# Revit family: XY 4 L
name_source: partatom
category: Generic Models
revit_build: Autodesk Revit 2017 (Build: 20170419_0315(x64)
units: mm (PartAtom-declared; Revit-internal decimal feet)

## family parameters
Always vertical = Yes
Can host rebar = No
Cut with Voids When Loaded = No
Host = Wall
Part Type = Normal
Room Calculation Point = No
Round Connector Dimension = Use Diameter
Shared = No

## types (1)
- XY 4 L
    Depth = 200 mm  [stored 0.656168 ft]
    EAN = 6430034743057
    Height = 870 mm
    IP = IP 34
    Keynote = 6120
    LVI = 5282083
    Leveys = 518 mm  [stored 1.69948 ft]
    Manufacturer = Sentakia Oy
    Materiaali = kiillotettu rst
    Model = XZ-4 L
    Sentakia_Material_Default = Stainless Steel, Polished_sentakia
    Sähkönumero = 8112505
    Teho = 50 W
    WEB = http://www.sentakia.com

note: [stored X ft] marks values corroborated as IEEE doubles in the binary element streams (Revit-internal decimal feet)

## geometry (parser evidence)
native form markers: Blend x4, Sweep x2
no freeform markers — native parametric forms only
